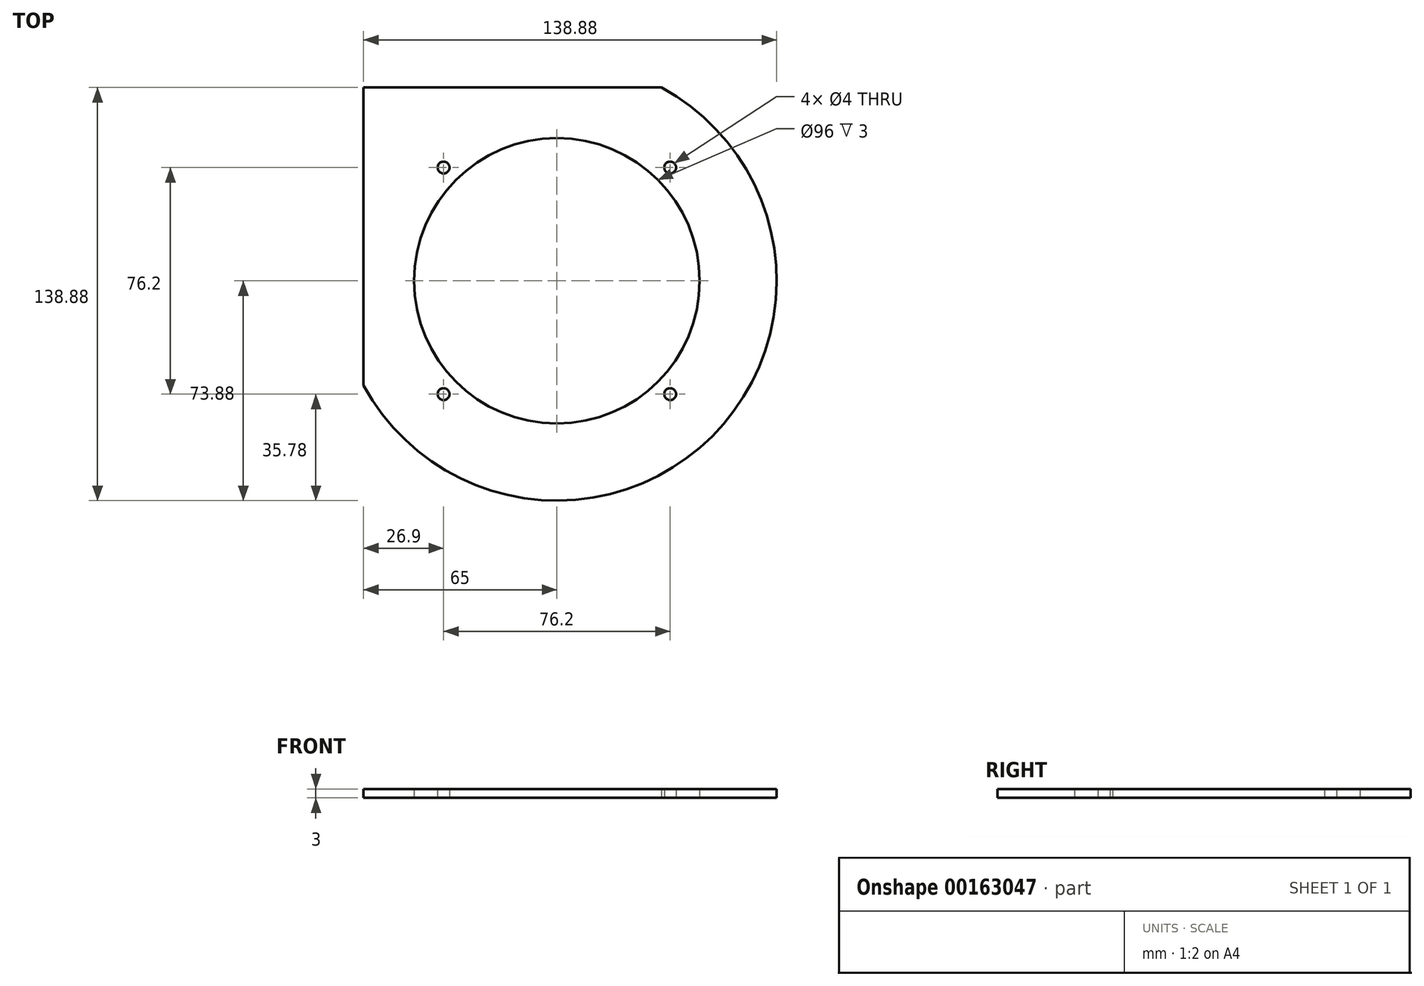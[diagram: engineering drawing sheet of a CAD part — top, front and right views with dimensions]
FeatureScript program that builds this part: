
annotation { "Feature Type Name" : "Feature", "Feature Type Description" : "" }
export const myFeature = defineFeature(function(context is Context, id is Id, definition is map)
    precondition{}
    {
        {
            var Q0;
            Q0=qCreatedBy(makeId("Top.planeOp"),FACE);
            var sketch = newSketch(context, id + "F0", { "sketchPlane" : qUnion([Q0])});
            skCircle(sketch, "E0", {"center": v(0, 0) * mm, "radius": 48 * mm});
            skArc(sketch, "E1", {"start": v(-65, -35.12) * mm, "mid": v(52.24, -52.24) * mm, "end": v(35.12, 65) * mm});
            skCircle(sketch, "E2", {"center": v(0, 0) * mm, "radius": 53.88 * mm, "construction": true});
            skCircle(sketch, "E3", {"center": v(-38.1, 38.1) * mm, "radius": 2 * mm});
            skCircle(sketch, "E4.1.0", {"center": v(-38.1, -38.1) * mm, "radius": 2 * mm});
            skCircle(sketch, "E4.2.0", {"center": v(38.1, -38.1) * mm, "radius": 2 * mm});
            skCircle(sketch, "E5.1.3.0", {"center": v(38.1, 38.1) * mm, "radius": 2 * mm});
            skLineSegment(sketch, "E6", {"start": v(0, 0) * mm, "end": v(102, 0) * mm, "construction": true});
            skLineSegment(sketch, "E7", {"start": v(0, 0) * mm, "end": v(38.1, -38.1) * mm, "construction": true});
            skCircle(sketch, "E8", {"center": v(38.1, -38.1) * mm, "radius": 5.5 * mm, "construction": true});
            skLineSegment(sketch, "E9.top", {"start": v(35.12, 65) * mm, "end": v(-65, 65) * mm});
            skLineSegment(sketch, "E9.right", {"start": v(-65, -35.12) * mm, "end": v(-65, 65) * mm});
            skPoint(sketch, "E10", {"position": v(-35.12, 65) * mm});
            skPoint(sketch, "E11", {"position": v(35.12, 65) * mm});
            skPoint(sketch, "E12.orphan", {"position": v(-65, -65) * mm});
            skPoint(sketch, "E13.orphan", {"position": v(65, -65) * mm});
            skPoint(sketch, "E9.left.end.orphan", {"position": v(65, 65) * mm});
            skSolve(sketch);
        }
        {
            var Q0;
            Q0 = qSketchRegion(id + "F0", true);
            var Q1;
            Q1=makeQuery(id+"F0.imprint","IMPRINT",FACE,{"disambiguationData":[TD([[makeQuery(id+"F0.imprint","IMPRINT",EDGE,{"derivedFrom":sQuery(id+"F0.wireOp",EDGE,"E0")}),-1.0]])]});
            extrude(context, id + "F1", {"entities" : qUnion([Q0, Q1]), "depth" : 3 * mm});
        }
    });
